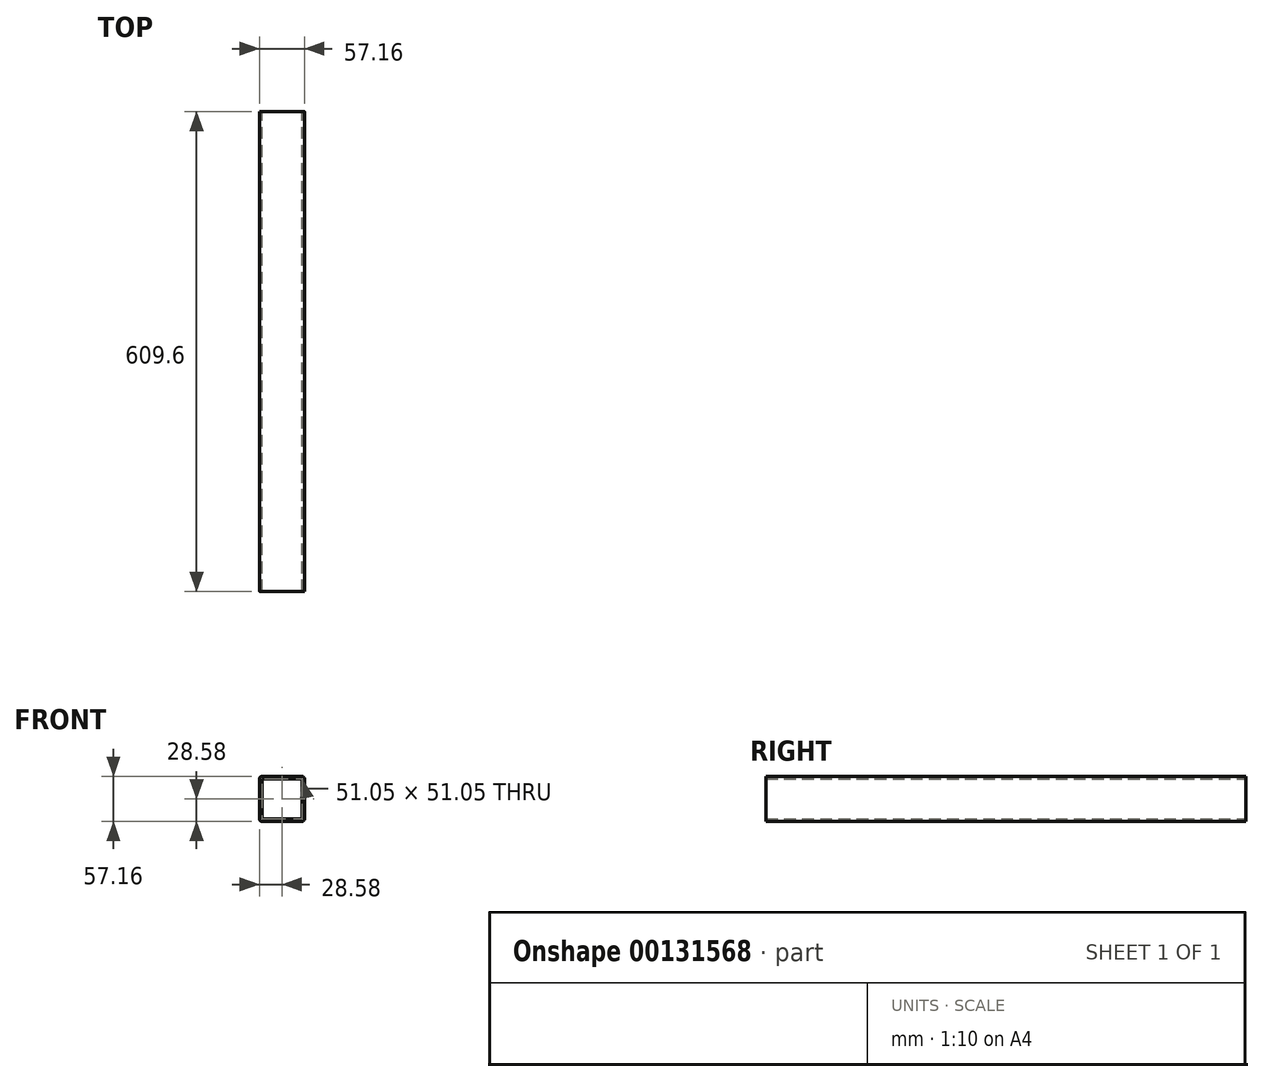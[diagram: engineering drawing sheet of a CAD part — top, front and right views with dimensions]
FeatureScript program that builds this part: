
annotation { "Feature Type Name" : "Feature", "Feature Type Description" : "" }
export const myFeature = defineFeature(function(context is Context, id is Id, definition is map)
    precondition{}
    {
        {
            var Q0;
            Q0=qCreatedBy(makeId("Front.planeOp"),FACE);
            var sketch = newSketch(context, id + "F0", { "sketchPlane" : qUnion([Q0])});
            skLineSegment(sketch, "E0.bottom", {"start": v(25.53, 28.58) * mm, "end": v(-25.53, 28.58) * mm});
            skLineSegment(sketch, "E0.top", {"start": v(25.53, -28.58) * mm, "end": v(-25.53, -28.58) * mm});
            skLineSegment(sketch, "E0.left", {"start": v(28.58, 25.53) * mm, "end": v(28.58, -25.53) * mm});
            skLineSegment(sketch, "E0.right", {"start": v(-28.58, 25.53) * mm, "end": v(-28.58, -25.53) * mm});
            skPoint(sketch, "E0.middle", {"position": v(0, 0) * mm});
            skLineSegment(sketch, "E1.bottom", {"start": v(25.53, 25.53) * mm, "end": v(-25.53, 25.53) * mm});
            skLineSegment(sketch, "E1.top", {"start": v(25.53, -25.53) * mm, "end": v(-25.53, -25.53) * mm});
            skLineSegment(sketch, "E1.left", {"start": v(25.53, 25.53) * mm, "end": v(25.53, -25.53) * mm});
            skLineSegment(sketch, "E1.right", {"start": v(-25.53, 25.53) * mm, "end": v(-25.53, -25.53) * mm});
            skPoint(sketch, "E2.visualSharp", {"position": v(-28.58, 28.58) * mm});
            skArc(sketch, "E2.filletArc", {"start": v(-25.53, 28.58) * mm, "mid": v(-27.68, 27.68) * mm, "end": v(-28.58, 25.53) * mm});
            skPoint(sketch, "E3.visualSharp", {"position": v(28.58, 28.58) * mm});
            skArc(sketch, "E3.filletArc", {"start": v(28.58, 25.53) * mm, "mid": v(27.68, 27.68) * mm, "end": v(25.53, 28.58) * mm});
            skPoint(sketch, "E4.visualSharp", {"position": v(28.58, -28.58) * mm});
            skArc(sketch, "E4.filletArc", {"start": v(25.53, -28.58) * mm, "mid": v(27.68, -27.68) * mm, "end": v(28.58, -25.53) * mm});
            skPoint(sketch, "E5.visualSharp", {"position": v(-28.58, -28.58) * mm});
            skArc(sketch, "E5.filletArc", {"start": v(-28.58, -25.53) * mm, "mid": v(-27.68, -27.68) * mm, "end": v(-25.53, -28.58) * mm});
            skSolve(sketch);
        }
        {
            var Q0;
            Q0=makeQuery(id+"F0.imprint","IMPRINT",FACE,{"disambiguationData":[TD([[makeQuery(id+"F0.imprint","IMPRINT",EDGE,{"derivedFrom":sQuery(id+"F0.wireOp",EDGE,"E0.bottom")}),1.0]])]});
            extrude(context, id + "F3", {"entities" : qUnion([Q0]), "depth" : 609.6 * mm});
        }
    });
